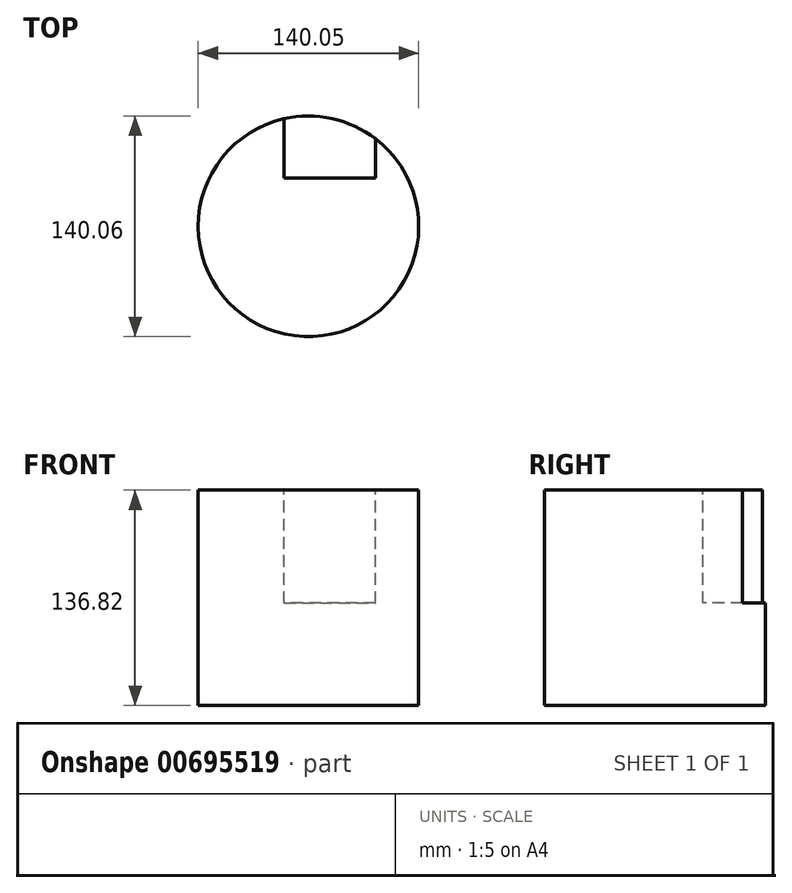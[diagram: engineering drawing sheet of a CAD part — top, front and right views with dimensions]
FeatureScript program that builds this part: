
annotation { "Feature Type Name" : "Feature", "Feature Type Description" : "" }
export const myFeature = defineFeature(function(context is Context, id is Id, definition is map)
    precondition{}
    {
        {
            var Q0;
            Q0=qCreatedBy(makeId("Top.planeOp"),FACE);
            var sketch = newSketch(context, id + "F0", { "sketchPlane" : qUnion([Q0])});
            skCircle(sketch, "E0", {"center": v(-99.52, -275.5) * mm, "radius": 70.03 * mm});
            skSolve(sketch);
        }
        {
            var Q0;
            Q0=makeQuery(id+"F0.imprint","IMPRINT",FACE,{"disambiguationData":[TD([[makeQuery(id+"F0.imprint","IMPRINT",EDGE,{"derivedFrom":sQuery(id+"F0.wireOp",EDGE,"E0")}),1.0]])]});
            var Q1;
            Q1=sQuery(id+"F0.wireOp",EDGE,"E0");
            extrude(context, id + "F1", {"entities" : qUnion([Q0]), "surfaceEntities" : qUnion([Q1]), "depth" : 136.82 * mm, "offsetDistance" : 25.4 * mm});
        }
        {
            var Q0;
            Q0=makeQuery(id+"F1.opExtrude","CAP_FACE",FACE,{"disambiguationData":[OSD([sQuery(id+"F0.wireOp",EDGE,"E0")])],"isStart":false});
            var sketch = newSketch(context, id + "F2", { "sketchPlane" : qUnion([Q0])});
            skLineSegment(sketch, "E1.bottom", {"start": v(-123.97, -244.94) * mm, "end": v(-116.16, -244.94) * mm});
            skLineSegment(sketch, "E1.top", {"start": v(-123.97, -240.45) * mm, "end": v(-116.16, -240.45) * mm});
            skLineSegment(sketch, "E1.left", {"start": v(-123.97, -244.94) * mm, "end": v(-123.97, -240.45) * mm});
            skLineSegment(sketch, "E1.right", {"start": v(-116.16, -244.94) * mm, "end": v(-116.16, -240.45) * mm});
            skLineSegment(sketch, "E2.bottom", {"start": v(-114.98, -186.65) * mm, "end": v(-56.97, -186.65) * mm});
            skLineSegment(sketch, "E2.top", {"start": v(-114.98, -244.94) * mm, "end": v(-56.97, -244.94) * mm});
            skLineSegment(sketch, "E2.left", {"start": v(-114.98, -186.65) * mm, "end": v(-114.98, -244.94) * mm});
            skLineSegment(sketch, "E2.right", {"start": v(-56.97, -186.65) * mm, "end": v(-56.97, -244.94) * mm});
            skSolve(sketch);
        }
        {
            var Q0;
            {var subQ0=sQuery(id+"F2.wireOp",EDGE,"E2.top");Q0=makeQuery(id+"F2.imprint","IMPRINT",FACE,{"disambiguationData":[TD([[makeQuery(id+"F2.imprint","IMPRINT",EDGE,{"derivedFrom":subQ0}),1.0]])]});}
            extrude(context, id + "F3", {"entities" : qUnion([Q0]), "operationType" : NewBodyOperationType.REMOVE, "oppositeDirection" : true, "depth" : 71.76 * mm, "offsetDistance" : 25.4 * mm});
        }
    });
